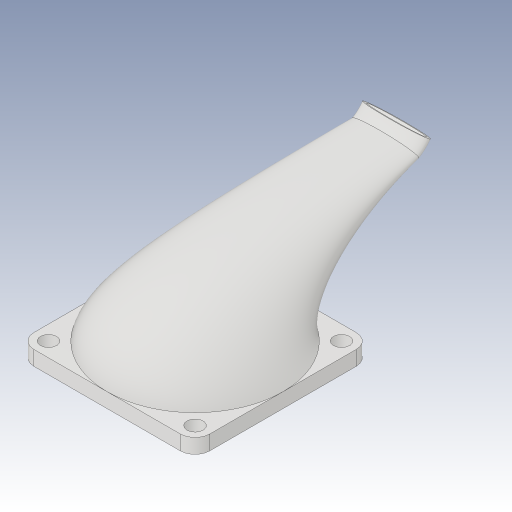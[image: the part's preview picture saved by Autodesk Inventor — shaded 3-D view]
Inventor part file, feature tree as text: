
AUTODESK INVENTOR PART (.ipt)
format: ipt  version: 2023.3 (Build 273359000, 359)  size: 415,744 bytes
history: native  units: in
note: dims shown in document units (in); Inventor stores cm internally (conversion verified against a paired STEP export)
features: sketch x5, plane x3, loft x2, extrude x1, sweep x1, projected_geometry x1
ambient origin geometry x8: Origin, YZ Plane, XZ Plane, XY Plane, X Axis, Y Axis, Z Axis, Center Point
bodies: Body1 (feature_tree)
feature tree (13):
  sketch  "Skizze3"  dims[d4=0.9449in d5=0.7874in]
  extrude  "Extrusion3"  Depth=0.7874in
  plane  "Arbeitsebene1"
  sketch  "Skizze6"  dims[d13=0.0787in d14=0.0in d15=0.5512in]
  plane  "Arbeitsebene3"
  sketch  "Skizze4"  dims[d6=0.1575in d7=0.0866in]
  plane  "Arbeitsebene2"
  sketch  "Skizze5"  dims[d8=1.5748in d10=360.0deg d12=0.8661in]
  loft  "Erhebung4"
  loft  "Erhebung5"
  sweep  "Sweeping1"
  projected_geometry  "Projizierte Kontur1"
  sketch  "Skizze8"  dims[d16=0.1575in d17=0.0394in d19=0.1772in d20=0.0551in d39=0.4331in d40=-0.2061in d41=0.0in d42=90.0deg d43=0.0in d44=90.0deg d45=0.0in d46=90.0deg d47=0.0in d48=90.0deg d49=0.0in d50=90.0deg d51=0.0in d52=90.0deg d53=0.0in d54=90.0deg d55=0.0in d56=90.0deg d57=0.4331in d58=0.1378in d63=0.4466in d65=0.0591in d66=0.0in d67=0.0in]
